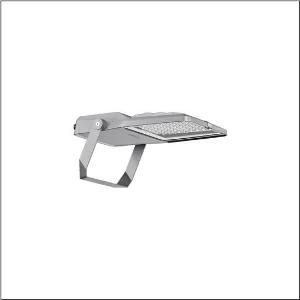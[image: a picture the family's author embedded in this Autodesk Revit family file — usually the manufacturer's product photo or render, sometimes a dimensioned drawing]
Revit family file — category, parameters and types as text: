
# Revit family: floodlight_fl_21_iq_mini___pl64_5xa7772d2e1a_f3f3
name_source: partatom
category: Lighting Fixtures
units: mm (PartAtom-declared; Revit-internal decimal feet)

## family parameters
Cut with Voids When Loaded = No
Host = Face
Light Source = No
Part Type = Normal
Room Calculation Point = No
Round Connector Dimension = Use Diameter
Shared = No

## types (1)
- --- (1 x LED, 17220 lm, 143 W, 3000K)
    Apparent Load = 143 VA
    CIE Flux Codes = 28 80 98 100 100
    Color Rendering = 70
    Color Temperature = 3000K
    Default Elevation = 1800 mm
    Description = Floodlight FL 21 iQ mini, floodlight, primary light control with lens, of PMMA, primary optical cover: protective disc, of toughened safety glass, transparent, light distribution: PL64, light emission: direct distribution, installation type: surface-mounted, lamps: LED, High Power LED, rated values: 17.220lm | 143W | 120,4lm/W (begin service life); end service life: 17.220lm | 151,6W; at 50% lumin. flux: 8.610lm | 60,6W | 142,1lm/W, colour temperature: 3000K, colour rendering: CRI > 70, light colour: 730, light setting 1 begin service life: 100% | 17.220lm | 143W | 120,4lm/W | 3.000K, light setting 1 end service life: 151,6W, further light settings possible, control: Street-Remote, Auto-Match, Temp-Guard, Night-Set, Smart-Wire, Desk-Remote (wireless, voltage-free reading and setting of iQ features in the workshop via application-optimized NFC function/RFID function), optimised constant luminous flux control (CLO 2.0), pre-setting: linear dimming characteristic, with terminal, 6-pole, mains connection: 220..240V, AC, 50/60Hz, luminaire housing, of diecast aluminium, powder-coated, SITECO metallic grey (DB 702S), corrosivity category C5 mid according to DIN EN ISO 12944suitable for swimming poolschlorine-resistant, sealing non-destructively replaceable, mounting bracket, of steel, galvanised, powder-coated, SITECO metallic grey (DB 702S), protection rating (complete): IP66, insulation class (complete): insulation class II (safety insulation), certification: CE, ENEC, VDE, protection symbol: D, impact resistance: IK08, permissible operating ambient temperature: -40..+40°C, permissible operating ambient temperature for outdoor applications: -40..+50°C, standard: DIN EN 12944, LABS conformity tested according to VDMA 24364:2018-05, packaging unit: 1 piece

Light Distribution: PL64
    Height = 70 mm
    Lamp = 1 x LED
    Lamp Light Flux = 17220 lm
    Lamp Power = 143 W
    Lamp count = 1
    Length = 485 mm
    Luminous efficacy = 120 lm/W
    Manufacturer = Siteco
    ModVariant = No
    Model = 5XA7772D2E1A
    Mounting Place = Pole
    Mounting Type = Pole annexe
    Number of Poles = 1
    OnlyDefault = Yes
    Power Factor = 1
    Product Name = Floodlight FL 21 iQ mini | PL64
    Product group = floodlight | pylon annexe
    ProductGroupID = 6201
    Protection Class = Protection class II
    Protection Degree = IP 66
    RLX_Detail_Level = 1
    RLX_Emergency_Light_Flux = 0 lm
    RLX_Emergency_Type = 0
    RLX_Emergency_Type_DB = No
    RlxData = <blob elided: 96749 chars, md5=960c095b>
    Socket = socket
    Standby Power = 0 W
    System Light Flux = 17220 lm
    System Power = 143 W
    Type Comments = factory setting: luminous flux: 100 % | dim-lin: 254 | 730 mA
    Type Image = l_1006845.jpg
    URL = http://relux.com
    VarID = @adj_166911
    Voltage = 0 V
    Weight = 0.00 kg
    Width = 337 mm

## geometry (parser evidence)
native form markers: Blend x4, Sweep x13
no freeform markers — native parametric forms only
